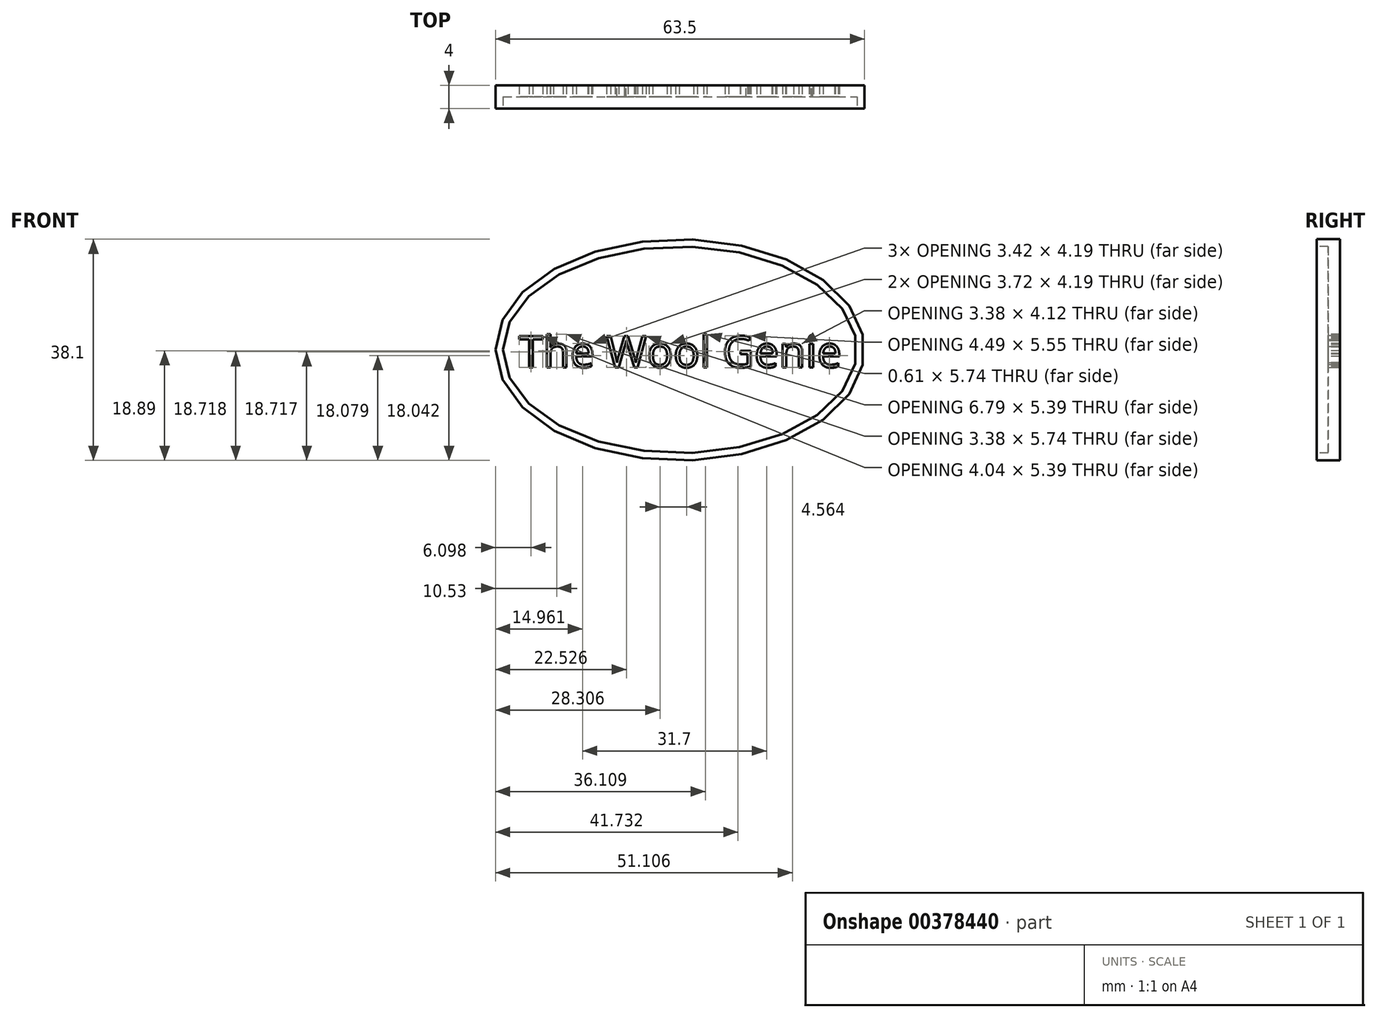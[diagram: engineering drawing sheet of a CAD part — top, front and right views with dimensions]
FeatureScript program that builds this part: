
annotation { "Feature Type Name" : "Feature", "Feature Type Description" : "" }
export const myFeature = defineFeature(function(context is Context, id is Id, definition is map)
    precondition{}
    {
        {
            var Q0;
            Q0=qCreatedBy(makeId("Front.planeOp"),FACE);
            var sketch = newSketch(context, id + "F0", { "sketchPlane" : qUnion([Q0])});
            skEllipse(sketch, "E0", {"center": v(0, 0) * mm, "majorRadius": 31.75 * mm, "minorRadius": 19.05 * mm, "majorAxis": v(-1, 0)});
            skSolve(sketch);
        }
        {
            var Q0;
            Q0=makeQuery(id+"F0.imprint","IMPRINT",FACE,{"disambiguationData":[TD([[makeQuery(id+"F0.imprint","IMPRINT",EDGE,{"derivedFrom":sQuery(id+"F0.wireOp",EDGE,"E0")}),1.0]])]});
            extrude(context, id + "F1", {"entities" : qUnion([Q0]), "depth" : 4 * mm});
        }
        {
            var Q0;
            Q0=makeQuery(id+"F1.opExtrude","CAP_FACE",FACE,{"disambiguationData":[OSD([sQuery(id+"F0.wireOp",EDGE,"E0")])],"isStart":false});
            var sketch = newSketch(context, id + "F2", { "sketchPlane" : qUnion([Q0])});
            skEllipse(sketch, "E1", {"center": v(0, 0) * mm, "majorRadius": 30.48 * mm, "minorRadius": 17.78 * mm, "majorAxis": v(-1, 0)});
            skSolve(sketch);
        }
        {
            var Q0;
            Q0=makeQuery(id+"F2.imprint","IMPRINT",FACE,{"disambiguationData":[TD([[makeQuery(id+"F2.imprint","IMPRINT",EDGE,{"derivedFrom":sQuery(id+"F2.wireOp",EDGE,"E1")}),1.0]])]});
            extrude(context, id + "F3", {"entities" : qUnion([Q0]), "operationType" : NewBodyOperationType.REMOVE, "oppositeDirection" : true, "depth" : 2 * mm});
        }
        {
            var Q0;
            Q0=makeQuery(id+"F3.boolean.opBoolean","COPY",FACE,{"derivedFrom":makeQuery(id+"F3.opExtrude","CAP_FACE",FACE,{"disambiguationData":[OSD([sQuery(id+"F2.wireOp",EDGE,"E1")])],"isStart":false})});
            var sketch = newSketch(context, id + "F4", { "sketchPlane" : qUnion([Q0])});
            skText(sketch, "E2", { "text": "The Wool Genie", "fontName": "OpenSans-Regular.ttf"});
            const initialGuessF4  = {"E2": [-0.02774, -0.00303, 1, 0, 0.00544]};
            skSetInitialGuess(sketch, initialGuessF4);
            skSolve(sketch);
        }
        {
            var Q0;
            Q0=qSketchRegion(id+"F4",true);
            extrude(context, id + "F5", {"entities" : qUnion([Q0]), "operationType" : NewBodyOperationType.REMOVE, "oppositeDirection" : true, "depth" : 2.54 * mm});
        }
    });
